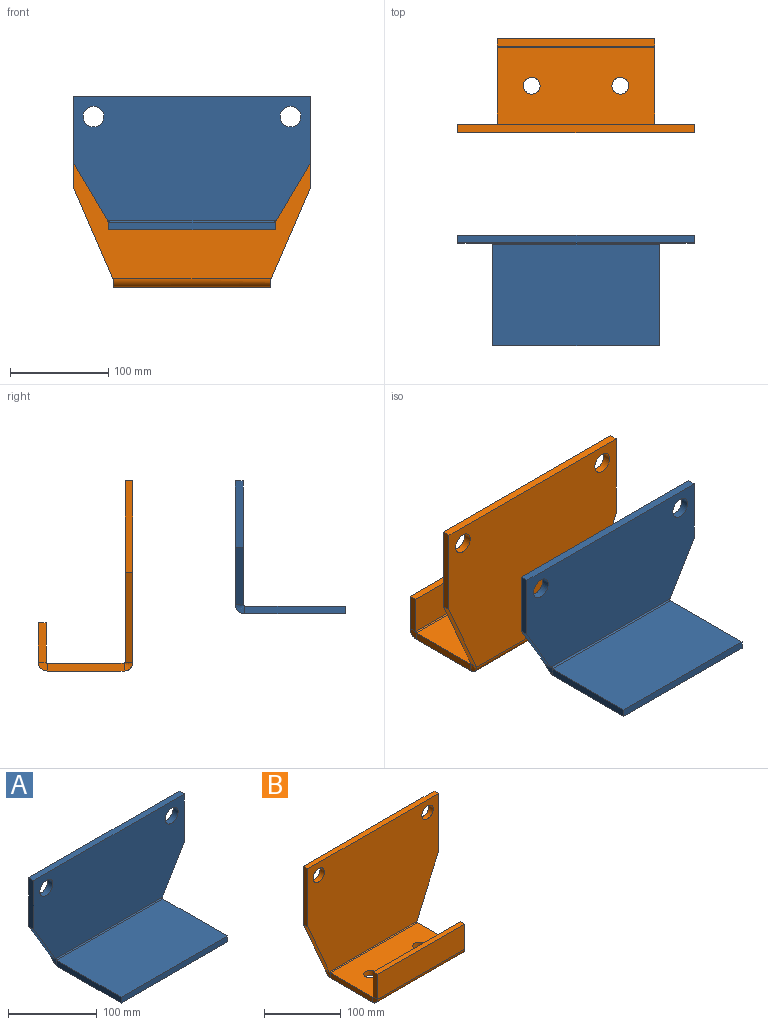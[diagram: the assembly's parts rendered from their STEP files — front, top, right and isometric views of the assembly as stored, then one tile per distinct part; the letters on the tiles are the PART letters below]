
ASSEMBLY  parts=2 mates=1
PART A: 18 faces, bbox 240x112x135 mm
  f0: plane 67.5x8mm, normal (-1,0,0), area 540mm2, adj f1,f6,f7,f8
  f1: plane 240x8mm, normal (0,0,1), area 1920mm2, adj f0,f2,f7,f8
  f2: plane 67.5x8mm, normal (1,0,0), area 540mm2, adj f1,f3,f7,f8
  f3: plane 58x34.37mm, normal (0.86,0,-0.51), area 539.4mm2, adj f2,f7,f8,f15
  f4: cylinder r=10.5mm len=21mm, axis (0,1,0), area 527.8mm2, adj f7,f8
  f5: cylinder r=10.5mm len=21mm, axis (0,1,0), area 527.8mm2, adj f7,f8
  f6: plane 58x34.37mm, normal (-0.86,0,-0.51), area 539.4mm2, adj f0,f7,f8,f14
  f7: plane 240x125.5mm, normal (0,1,0), area 27433.8mm2, adj f0,f1,f2,f3,f4,f5,f6,f16
  f8: plane 240x125.5mm, normal (0,-1,0), area 27433.8mm2, adj f0,f1,f2,f3,f4,f5,f6,f17
  f9: plane 169.48x8mm, normal (0,-1,0), area 1355.9mm2, adj f10,f11,f12,f13
  f10: plane 102.5x8mm, normal (-1,0,0), area 820mm2, adj f9,f12,f13,f14
  f11: plane 102.5x8mm, normal (1,0,0), area 820mm2, adj f9,f12,f13,f15
  f12: plane 169.48x102.5mm, normal (0,0,-1), area 17371.9mm2, adj f9,f10,f11,f16
  f13: plane 169.48x102.5mm, normal (0,0,1), area 17371.9mm2, adj f9,f10,f11,f17
  f14: bspline ~9.5x9.5mm, area 73.1mm2, adj f6,f10,f16,f17
  f15: bspline ~9.5x9.5mm, area 73.2mm2, adj f3,f11,f16,f17
  f16: cylinder r=9.5mm len=171.26mm, axis (-1,0,0), area 2519.9mm2, adj f7,f12,f14,f15
  f17: cylinder r=1.5mm len=171.26mm, axis (-1,0,0), area 397.9mm2, adj f8,f13,f14,f15
PART B: 28 faces, bbox 240x96x193 mm
  f0: plane 92.5x8mm, normal (-1,0,0), area 740mm2, adj f1,f6,f7,f8
  f1: plane 240x8mm, normal (0,0,1), area 1920mm2, adj f0,f2,f7,f8
  f2: plane 92.5x8mm, normal (1,0,0), area 740mm2, adj f1,f3,f7,f8
  f3: plane 91.48x39.56mm, normal (0.92,0,-0.4), area 797.3mm2, adj f2,f7,f8,f24
  f4: cylinder r=10.5mm len=21mm, axis (0,1,0), area 527.8mm2, adj f7,f8
  f5: cylinder r=10.5mm len=21mm, axis (0,1,0), area 527.8mm2, adj f7,f8
  f6: plane 91.48x39.56mm, normal (-0.92,0,-0.4), area 797.3mm2, adj f0,f7,f8,f25
  f7: plane 240x183.98mm, normal (0,1,0), area 39843.6mm2, adj f0,f1,f2,f3,f4,f5,f6,f26
  f8: plane 240x183.98mm, normal (0,-1,0), area 39843.6mm2, adj f0,f1,f2,f3,f4,f5,f6,f27
  f9: plane 77.97x8mm, normal (-1,0,0), area 623.8mm2, adj f13,f14,f21,f25
  f10: cylinder r=8.5mm len=17mm, axis (0,0,-1), area 427.3mm2, adj f13,f14
  f11: cylinder r=8.5mm len=17mm, axis (0,0,-1), area 427.3mm2, adj f13,f14
  f12: plane 77.97x8mm, normal (1,0,0), area 623.8mm2, adj f13,f14,f20,f24
  f13: plane 160x77.97mm, normal (0,0,-1), area 12021.2mm2, adj f9,f10,f11,f12,f22,f26
  f14: plane 160x77.97mm, normal (0,0,1), area 12021.2mm2, adj f9,f10,f11,f12,f23,f27
  f15: plane 160x8mm, normal (0,0,1), area 1280mm2, adj f16,f17,f18,f19
  f16: plane 39.99x8mm, normal (-1,0,0), area 319.9mm2, adj f15,f18,f19,f21
  f17: plane 39.99x8mm, normal (1,0,0), area 319.9mm2, adj f15,f18,f19,f20
  f18: plane 160x39.99mm, normal (0,-1,0), area 6398.4mm2, adj f15,f16,f17,f22
  f19: plane 160x39.99mm, normal (0,1,0), area 6398.4mm2, adj f15,f16,f17,f23
  f20: plane 9.01x9.01mm, normal (1,0,0), area 63mm2, adj f12,f17,f22,f23
  f21: plane 9.01x9.01mm, normal (-1,0,0), area 63mm2, adj f9,f16,f22,f23
  f22: cylinder r=9.01mm len=160mm, axis (1,0,0), area 2264.5mm2, adj f13,f18,f20,f21
  f23: cylinder r=1.01mm len=160mm, axis (1,0,0), area 253.8mm2, adj f14,f19,f20,f21
  f24: bspline ~9.02x9.02mm, area 65.4mm2, adj f3,f12,f26,f27
  f25: bspline ~9.02x9.02mm, area 65.3mm2, adj f6,f9,f26,f27
  f26: cylinder r=9.02mm len=160.88mm, axis (1,0,0), area 2258.3mm2, adj f7,f13,f24,f25
  f27: cylinder r=1.02mm len=160.88mm, axis (1,0,0), area 255.4mm2, adj f8,f14,f24,f25
PLACE A t=(38.22,162.39,-28.94)mm
PLACE B rot(axis=(0,0,1),180deg) t=(278.22,282.39,-78.94)mm
MATE fastened B.f4 <-> A.f5  axis (0,1,0) through (258.22,282.39,86.06)mm
